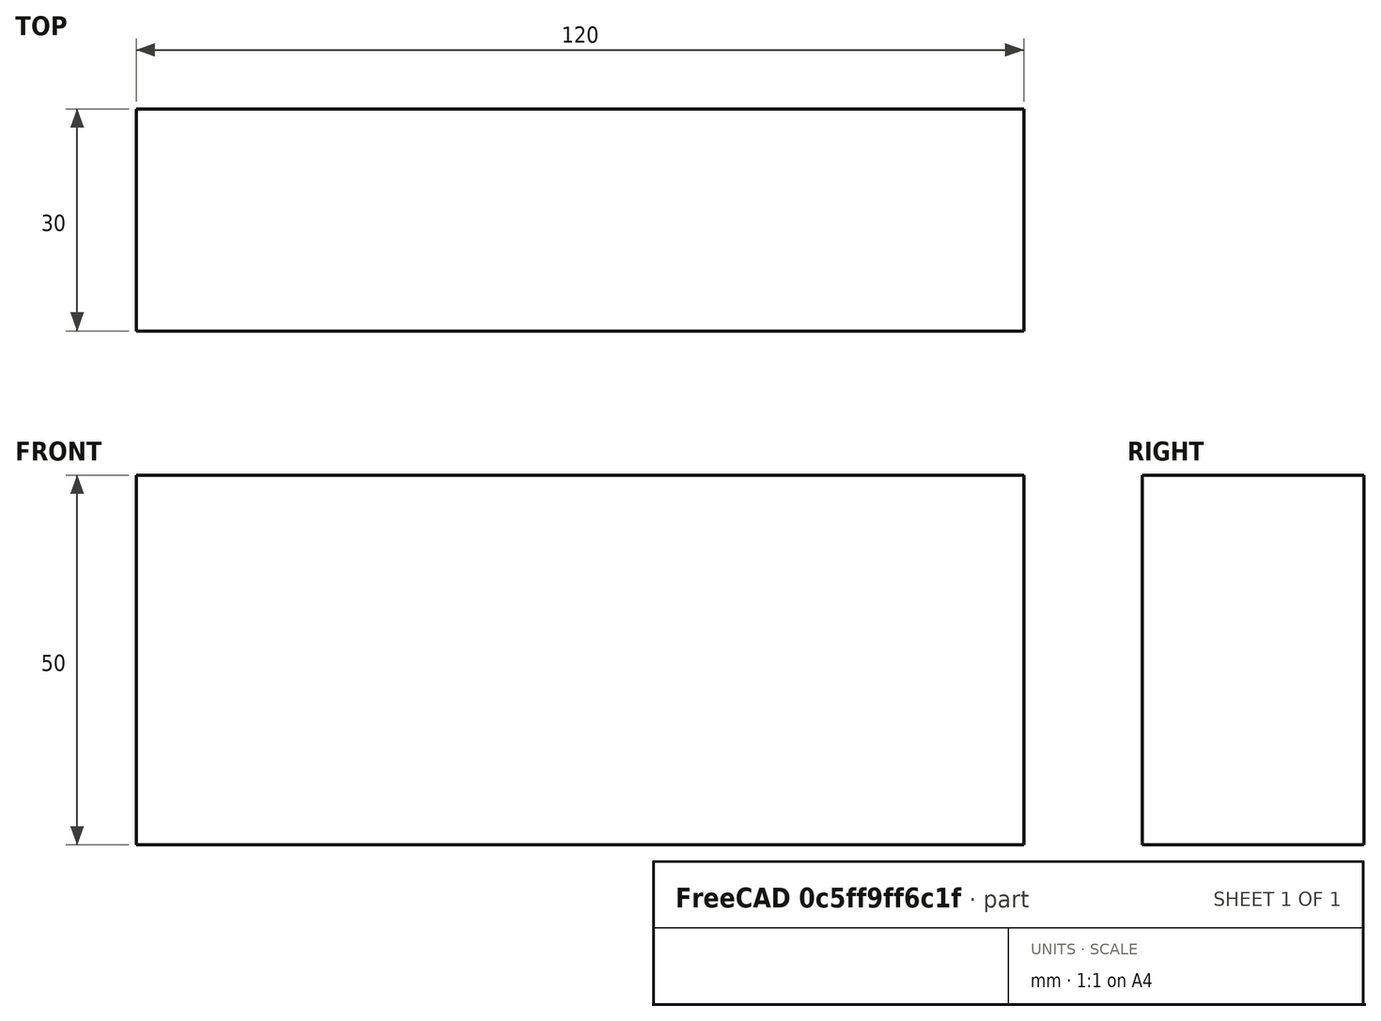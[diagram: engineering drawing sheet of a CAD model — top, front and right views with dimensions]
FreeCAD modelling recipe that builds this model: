
FCSTD DOCUMENT  (FreeCAD 0.15R4671 (Git))
Label: Flat Bar 120x30 EN10058 S235JR
License: All rights reserved
LicenseURL: http://en.wikipedia.org/wiki/All_rights_reserved
objects: Sketcher::SketchObject×1, Part::Extrusion×1
note: 2 computed .brp shape members not serialized (recipe doc carries the construction recipe); baked Part::Feature solids carry a one-line shape summary decoded from their .brp

FEATURE [Sketcher::SketchObject] Sketch
  sketch-geometry (4):
    g0: LineSegment StartX=-60 StartY=-15 StartZ=0 EndX=60 EndY=-15 EndZ=0
    g1: LineSegment StartX=60 StartY=-15 StartZ=0 EndX=60 EndY=15 EndZ=0
    g2: LineSegment StartX=60 StartY=15 StartZ=0 EndX=-60 EndY=15 EndZ=0
    g3: LineSegment StartX=-60 StartY=15 StartZ=0 EndX=-60 EndY=-15 EndZ=0
  constraints (12):
    c: Coincident(g0,g1)
    c: Coincident(g1,g2)
    c: Coincident(g2,g3)
    c: Coincident(g3,g0)
    c: Horizontal(g0)
    c: Horizontal(g2)
    c: Vertical(g1)
    c: Vertical(g3)
    c: Symmetric(g1,g2,g-2)
    c: Symmetric(g0,g1,g-1)
    c: DistanceY(g1) = 30
    c: DistanceX(g0) = 120
FEATURE [Part::Extrusion] Extrude  label="Flat Bar 120x30 EN10058 S235JR"
  Base = -> Sketch
  Dir = (0,0,50)
  Solid = true
